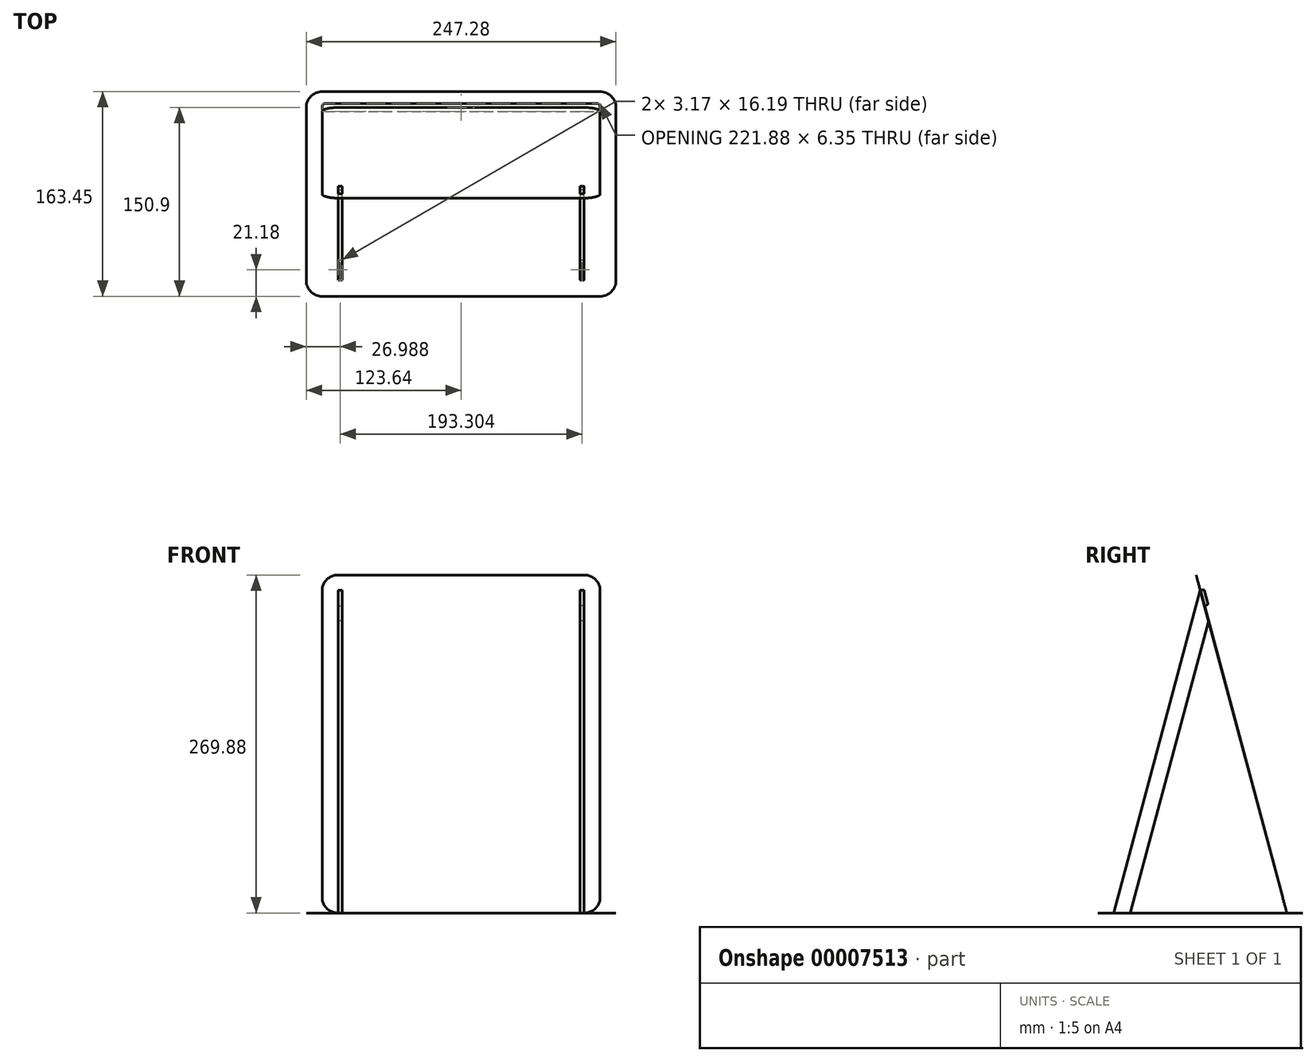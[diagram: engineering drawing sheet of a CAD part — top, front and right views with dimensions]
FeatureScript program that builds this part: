
annotation { "Feature Type Name" : "Feature", "Feature Type Description" : "" }
export const myFeature = defineFeature(function(context is Context, id is Id, definition is map)
    precondition{}
    {
        {
            var Q0;
            Q0=qCreatedBy(makeId("Right.planeOp"),FACE);
            var sketch = newSketch(context, id + "F0", { "sketchPlane" : qUnion([Q0])});
            skLineSegment(sketch, "E0", {"start": v(-72.31, 0) * mm, "end": v(72.31, 0) * mm});
            skLineSegment(sketch, "E1", {"start": v(72.31, 0) * mm, "end": v(0, 269.88) * mm});
            skLineSegment(sketch, "E2", {"start": v(0, 269.88) * mm, "end": v(-72.31, 0) * mm});
            skLineSegment(sketch, "E3", {"start": v(0, 269.88) * mm, "end": v(3.29, 257.61) * mm});
            skLineSegment(sketch, "E4", {"start": v(3.29, 257.61) * mm, "end": v(6.57, 245.35) * mm});
            skLineSegment(sketch, "E5", {"start": v(6.57, 245.35) * mm, "end": v(9.86, 233.08) * mm});
            skLineSegment(sketch, "E6", {"start": v(-72.31, 0) * mm, "end": v(-78.44, 0) * mm});
            skLineSegment(sketch, "E7", {"start": v(72.31, 0) * mm, "end": v(85.01, 0) * mm});
            skLineSegment(sketch, "E8", {"start": v(3.29, 257.61) * mm, "end": v(-65.74, 0) * mm, "construction": true});
            skSolve(sketch);
        }
        {
            var Q0;
            Q0=sQuery(id+"F0.wireOp",EDGE,"E1");
            cPlane(context, id + "F1", {"entities" : qUnion([Q0]), "cplaneType" : CPlaneType.LINE_ANGLE, "offset" : 152.4 * mm, "angle" : 90 * degree, "width" : 152.4 * mm, "height" : 152.4 * mm});
        }
        {
            var Q0;
            Q0=qCreatedBy(id+"F1.planeOp",FACE);
            var sketch = newSketch(context, id + "F2", { "sketchPlane" : qUnion([Q0])});
            skPoint(sketch, "E9.0", {"position": v(0, -18.72) * mm});
            skPoint(sketch, "E9.1", {"position": v(0, 260.68) * mm});
            skLineSegment(sketch, "E10.bottom", {"start": v(-98.24, 260.68) * mm, "end": v(98.24, 260.68) * mm});
            skLineSegment(sketch, "E10.top", {"start": v(-98.24, -18.72) * mm, "end": v(98.24, -18.72) * mm});
            skLineSegment(sketch, "E10.left", {"start": v(-110.94, 247.98) * mm, "end": v(-110.94, -6.02) * mm});
            skLineSegment(sketch, "E10.right", {"start": v(110.94, 247.98) * mm, "end": v(110.94, -6.02) * mm});
            skPoint(sketch, "E11.visualSharp", {"position": v(-110.94, 260.68) * mm});
            skArc(sketch, "E11.filletArc", {"start": v(-98.24, 260.68) * mm, "mid": v(-107.22, 256.96) * mm, "end": v(-110.94, 247.98) * mm});
            skPoint(sketch, "E12.visualSharp", {"position": v(110.94, 260.68) * mm});
            skArc(sketch, "E12.filletArc", {"start": v(110.94, 247.98) * mm, "mid": v(107.22, 256.96) * mm, "end": v(98.24, 260.68) * mm});
            skPoint(sketch, "E13.visualSharp", {"position": v(110.94, -18.72) * mm});
            skArc(sketch, "E13.filletArc", {"start": v(98.24, -18.72) * mm, "mid": v(107.22, -15) * mm, "end": v(110.94, -6.02) * mm});
            skPoint(sketch, "E14.visualSharp", {"position": v(-110.94, -18.72) * mm});
            skArc(sketch, "E14.filletArc", {"start": v(-110.94, -6.02) * mm, "mid": v(-107.22, -15) * mm, "end": v(-98.24, -18.72) * mm});
            skPoint(sketch, "E15.0", {"position": v(0, 247.98) * mm});
            skPoint(sketch, "E15.1", {"position": v(0, 235.28) * mm});
            skLineSegment(sketch, "E16", {"start": v(-98.24, 247.98) * mm, "end": v(98.24, 247.98) * mm, "construction": true});
            skLineSegment(sketch, "E17", {"start": v(-98.24, 235.28) * mm, "end": v(98.24, 235.28) * mm, "construction": true});
            skLineSegment(sketch, "E18", {"start": v(-98.24, 235.28) * mm, "end": v(-98.24, 247.98) * mm});
            skLineSegment(sketch, "E19", {"start": v(-98.24, 235.28) * mm, "end": v(-95.06, 235.28) * mm});
            skLineSegment(sketch, "E20", {"start": v(-95.06, 235.28) * mm, "end": v(-95.06, 247.98) * mm});
            skLineSegment(sketch, "E21", {"start": v(-95.06, 247.98) * mm, "end": v(-98.24, 247.98) * mm});
            skLineSegment(sketch, "E22", {"start": v(98.24, 247.98) * mm, "end": v(98.24, 235.28) * mm});
            skLineSegment(sketch, "E23", {"start": v(98.24, 235.28) * mm, "end": v(95.06, 235.28) * mm});
            skLineSegment(sketch, "E24", {"start": v(95.06, 235.28) * mm, "end": v(95.06, 247.98) * mm});
            skLineSegment(sketch, "E25", {"start": v(95.06, 247.98) * mm, "end": v(98.24, 247.98) * mm});
            skSolve(sketch);
        }
        {
            var Q0;
            Q0=makeQuery(id+"F2.imprint","IMPRINT",FACE,{"disambiguationData":[TD([[makeQuery(id+"F2.imprint","IMPRINT",EDGE,{"derivedFrom":sQuery(id+"F2.wireOp",EDGE,"E10.bottom")}),-1.0]])]});
            extrude(context, id + "F3", {"entities" : qUnion([Q0]), "depth" : 1 / 203.2 * mm});
        }
        {
            var Q0;
            Q0=makeQuery(id+"F3.opExtrude","CAP_EDGE",EDGE,{"disambiguationData":[OSD([sQuery(id+"F2.wireOp",EDGE,"E18")])],"isStart":true});
            cPlane(context, id + "F4", {"entities" : qUnion([Q0]), "cplaneType" : CPlaneType.LINE_ANGLE, "offset" : 152.4 * mm, "angle" : 0 * degree, "width" : 152.4 * mm, "height" : 152.4 * mm});
        }
        {
            var Q0;
            Q0=qCreatedBy(id+"F4.planeOp",FACE);
            var sketch = newSketch(context, id + "F5", { "sketchPlane" : qUnion([Q0])});
            skPoint(sketch, "E26.0", {"position": v(3.29, 257.61) * mm});
            skPoint(sketch, "E26.1", {"position": v(6.57, 245.35) * mm});
            skPoint(sketch, "E26.2", {"position": v(9.86, 233.08) * mm});
            skLineSegment(sketch, "E26.3", {"start": v(-72.31, 0) * mm, "end": v(72.31, 0) * mm, "construction": true});
            skLineSegment(sketch, "E26.4", {"start": v(0, 269.88) * mm, "end": v(-72.31, 0) * mm, "construction": true});
            skLineSegment(sketch, "E27.0", {"start": v(5.13, 258.1) * mm, "end": v(4, 257.8) * mm});
            skLineSegment(sketch, "E28", {"start": v(6.68, 257.2) * mm, "end": v(9.31, 247.4) * mm});
            skLineSegment(sketch, "E29", {"start": v(6.57, 245.35) * mm, "end": v(8.41, 245.84) * mm});
            skLineSegment(sketch, "E30", {"start": v(6.57, 245.35) * mm, "end": v(9.77, 233.4) * mm});
            skLineSegment(sketch, "E31", {"start": v(3.1, 256.9) * mm, "end": v(-65.31, 1.6) * mm});
            skLineSegment(sketch, "E32", {"start": v(-64.08, 0) * mm, "end": v(-53.57, 0) * mm});
            skLineSegment(sketch, "E33", {"start": v(-52.34, 0.94) * mm, "end": v(9.77, 232.75) * mm});
            skPoint(sketch, "E34.visualSharp", {"position": v(6.35, 258.43) * mm});
            skArc(sketch, "E34.filletArc", {"start": v(6.68, 257.2) * mm, "mid": v(6.1, 257.98) * mm, "end": v(5.13, 258.1) * mm});
            skPoint(sketch, "E35.visualSharp", {"position": v(9.64, 246.17) * mm});
            skArc(sketch, "E35.filletArc", {"start": v(8.41, 245.84) * mm, "mid": v(9.19, 246.43) * mm, "end": v(9.31, 247.4) * mm});
            skArc(sketch, "E36.filletArc", {"start": v(9.77, 232.75) * mm, "mid": v(9.82, 233.08) * mm, "end": v(9.77, 233.4) * mm});
            skPoint(sketch, "E37.visualSharp", {"position": v(-52.6, 0) * mm});
            skArc(sketch, "E37.filletArc", {"start": v(-53.57, 0) * mm, "mid": v(-52.8, 0.26) * mm, "end": v(-52.34, 0.94) * mm});
            skLineSegment(sketch, "E38", {"start": v(3.1, 256.9) * mm, "end": v(3.29, 257.61) * mm});
            skLineSegment(sketch, "E39", {"start": v(3.29, 257.61) * mm, "end": v(4, 257.8) * mm});
            skPoint(sketch, "E40.visualSharp", {"position": v(-65.74, 0) * mm});
            skArc(sketch, "E40.filletArc", {"start": v(-65.31, 1.6) * mm, "mid": v(-65.1, 0.5) * mm, "end": v(-64.08, 0) * mm});
            skSolve(sketch);
        }
        {
            var Q0;
            Q0 = qSketchRegion(id + "F5", true);
            var Q1;
            Q1=makeQuery(id+"F3.opExtrude","SWEPT_FACE",FACE,{"disambiguationData":[OSD([sQuery(id+"F2.wireOp",EDGE,"E20")])]});
            extrude(context, id + "F6", {"entities" : qUnion([Q0]), "operationType" : NewBodyOperationType.ADD, "endBound" : BoundingType.UP_TO_SURFACE, "oppositeDirection" : true, "endBoundEntityFace" : qUnion([Q1]), "depth" : 1 / 203.2 * mm});
        }
        {
            var Q0;
            Q0=makeQuery(id+"F3.opExtrude","CAP_EDGE",EDGE,{"disambiguationData":[OSD([sQuery(id+"F2.wireOp",EDGE,"E24")])],"isStart":true});
            cPlane(context, id + "F7", {"entities" : qUnion([Q0]), "cplaneType" : CPlaneType.LINE_ANGLE, "offset" : 152.4 * mm, "angle" : 0 * degree, "width" : 152.4 * mm, "height" : 152.4 * mm});
        }
        {
            var Q0;
            Q0=qCreatedBy(id+"F7.planeOp",FACE);
            var sketch = newSketch(context, id + "F8", { "sketchPlane" : qUnion([Q0])});
            skLineSegment(sketch, "E41.21", {"start": v(3.1, 256.9) * mm, "end": v(3.29, 257.61) * mm});
            skPoint(sketch, "E42.0", {"position": v(3.29, 257.61) * mm});
            skPoint(sketch, "E42.1", {"position": v(6.57, 245.35) * mm});
            skPoint(sketch, "E42.2", {"position": v(9.86, 233.08) * mm});
            skLineSegment(sketch, "E42.3", {"start": v(-72.31, 0) * mm, "end": v(72.31, 0) * mm});
            skLineSegment(sketch, "E42.4", {"start": v(0, 269.88) * mm, "end": v(-72.31, 0) * mm});
            skLineSegment(sketch, "E42.5", {"start": v(5.13, 258.1) * mm, "end": v(4, 257.8) * mm});
            skLineSegment(sketch, "E42.6", {"start": v(6.68, 257.2) * mm, "end": v(9.31, 247.4) * mm});
            skLineSegment(sketch, "E42.7", {"start": v(6.57, 245.35) * mm, "end": v(8.41, 245.84) * mm});
            skLineSegment(sketch, "E42.8", {"start": v(6.57, 245.35) * mm, "end": v(9.77, 233.4) * mm});
            skLineSegment(sketch, "E42.9", {"start": v(3.1, 256.9) * mm, "end": v(-65.31, 1.6) * mm});
            skLineSegment(sketch, "E42.10", {"start": v(-64.08, 0) * mm, "end": v(-53.57, 0) * mm});
            skLineSegment(sketch, "E42.11", {"start": v(-52.34, 0.94) * mm, "end": v(9.77, 232.75) * mm});
            skPoint(sketch, "E42.12", {"position": v(3.29, 257.61) * mm});
            skPoint(sketch, "E42.13", {"position": v(6.35, 258.43) * mm});
            skArc(sketch, "E42.14", {"start": v(6.68, 257.2) * mm, "mid": v(6.1, 257.98) * mm, "end": v(5.13, 258.1) * mm});
            skPoint(sketch, "E42.15", {"position": v(9.64, 246.17) * mm});
            skArc(sketch, "E42.16", {"start": v(8.41, 245.84) * mm, "mid": v(9.19, 246.43) * mm, "end": v(9.31, 247.4) * mm});
            skPoint(sketch, "E42.17", {"position": v(9.86, 233.08) * mm});
            skArc(sketch, "E42.18", {"start": v(9.77, 232.75) * mm, "mid": v(9.82, 233.08) * mm, "end": v(9.77, 233.4) * mm});
            skPoint(sketch, "E42.19", {"position": v(-52.6, 0) * mm});
            skArc(sketch, "E42.20", {"start": v(-53.57, 0) * mm, "mid": v(-52.8, 0.26) * mm, "end": v(-52.34, 0.94) * mm});
            skLineSegment(sketch, "E42.22", {"start": v(3.29, 257.61) * mm, "end": v(4, 257.8) * mm});
            skPoint(sketch, "E42.23", {"position": v(-65.74, 0) * mm});
            skArc(sketch, "E42.24", {"start": v(-65.31, 1.6) * mm, "mid": v(-65.1, 0.5) * mm, "end": v(-64.08, 0) * mm});
            skSolve(sketch);
        }
        {
            var Q0;
            Q0 = qSketchRegion(id + "F8", true);
            var Q1;
            Q1=makeQuery(id+"F3.opExtrude","SWEPT_FACE",FACE,{"disambiguationData":[OSD([sQuery(id+"F2.wireOp",EDGE,"E22")])]});
            extrude(context, id + "F9", {"entities" : qUnion([Q0]), "operationType" : NewBodyOperationType.ADD, "endBound" : BoundingType.UP_TO_SURFACE, "oppositeDirection" : true, "endBoundEntityFace" : qUnion([Q1]), "depth" : 3.17 * mm});
        }
        {
            var Q0;
            Q0=qCreatedBy(makeId("Top.planeOp"),FACE);
            var sketch = newSketch(context, id + "F10", { "sketchPlane" : qUnion([Q0])});
            skPoint(sketch, "E43.2", {"position": v(0, 85.01) * mm});
            skPoint(sketch, "E43.3", {"position": v(0, -78.44) * mm});
            skLineSegment(sketch, "E44.bottom", {"start": v(-110.94, -78.44) * mm, "end": v(110.94, -78.44) * mm});
            skLineSegment(sketch, "E44.top", {"start": v(-110.94, 85.01) * mm, "end": v(110.94, 85.01) * mm});
            skLineSegment(sketch, "E44.left", {"start": v(-123.64, -65.74) * mm, "end": v(-123.64, 72.31) * mm});
            skLineSegment(sketch, "E44.right", {"start": v(123.64, -65.74) * mm, "end": v(123.64, 72.31) * mm});
            skPoint(sketch, "E45.visualSharp", {"position": v(-123.64, -78.44) * mm});
            skArc(sketch, "E45.filletArc", {"start": v(-123.64, -65.74) * mm, "mid": v(-119.92, -74.72) * mm, "end": v(-110.94, -78.44) * mm});
            skPoint(sketch, "E46.visualSharp", {"position": v(123.64, -78.44) * mm});
            skArc(sketch, "E46.filletArc", {"start": v(110.94, -78.44) * mm, "mid": v(119.92, -74.72) * mm, "end": v(123.64, -65.74) * mm});
            skPoint(sketch, "E47.visualSharp", {"position": v(123.64, 85.01) * mm});
            skArc(sketch, "E47.filletArc", {"start": v(123.64, 72.31) * mm, "mid": v(119.92, 81.3) * mm, "end": v(110.94, 85.01) * mm});
            skPoint(sketch, "E48.visualSharp", {"position": v(-123.64, 85.01) * mm});
            skArc(sketch, "E48.filletArc", {"start": v(-110.94, 85.01) * mm, "mid": v(-119.92, 81.3) * mm, "end": v(-123.64, 72.31) * mm});
            skLineSegment(sketch, "E49.0", {"start": v(98.24, 75.38) * mm, "end": v(-98.24, 75.38) * mm, "construction": true});
            skLineSegment(sketch, "E50.bottom", {"start": v(-108.4, 69.28) * mm, "end": v(108.4, 69.28) * mm});
            skLineSegment(sketch, "E50.top", {"start": v(-108.4, 75.63) * mm, "end": v(108.4, 75.63) * mm});
            skLineSegment(sketch, "E50.left", {"start": v(-110.94, 71.82) * mm, "end": v(-110.94, 73.1) * mm});
            skLineSegment(sketch, "E50.right", {"start": v(110.94, 71.82) * mm, "end": v(110.94, 73.1) * mm});
            skPoint(sketch, "E51.visualSharp", {"position": v(-110.94, 69.28) * mm});
            skArc(sketch, "E51.filletArc", {"start": v(-110.94, 71.82) * mm, "mid": v(-110.2, 70.03) * mm, "end": v(-108.4, 69.28) * mm});
            skPoint(sketch, "E52.visualSharp", {"position": v(-110.94, 75.63) * mm});
            skArc(sketch, "E52.filletArc", {"start": v(-108.4, 75.63) * mm, "mid": v(-110.2, 74.9) * mm, "end": v(-110.94, 73.1) * mm});
            skPoint(sketch, "E53.visualSharp", {"position": v(110.94, 75.63) * mm});
            skArc(sketch, "E53.filletArc", {"start": v(110.94, 73.1) * mm, "mid": v(110.2, 74.9) * mm, "end": v(108.4, 75.63) * mm});
            skPoint(sketch, "E54.visualSharp", {"position": v(110.94, 69.28) * mm});
            skArc(sketch, "E54.filletArc", {"start": v(108.4, 69.28) * mm, "mid": v(110.2, 70.03) * mm, "end": v(110.94, 71.82) * mm});
            skLineSegment(sketch, "E55.0", {"start": v(-98.24, -64.08) * mm, "end": v(-98.24, -65.35) * mm});
            skLineSegment(sketch, "E55.1", {"start": v(-95.06, -64.08) * mm, "end": v(-95.06, -65.35) * mm});
            skLineSegment(sketch, "E55.2", {"start": v(-95.06, -64.08) * mm, "end": v(-95.06, -53.57) * mm});
            skLineSegment(sketch, "E55.3", {"start": v(-95.06, -52.34) * mm, "end": v(-95.06, -53.57) * mm});
            skLineSegment(sketch, "E55.4", {"start": v(-98.24, -64.08) * mm, "end": v(-98.24, -53.57) * mm});
            skLineSegment(sketch, "E55.5", {"start": v(-98.24, -52.34) * mm, "end": v(-98.24, -53.57) * mm});
            skLineSegment(sketch, "E56", {"start": v(-98.24, -65.35) * mm, "end": v(-95.06, -65.35) * mm});
            skLineSegment(sketch, "E57", {"start": v(-98.24, -52.34) * mm, "end": v(-98.24, -49.16) * mm});
            skLineSegment(sketch, "E58", {"start": v(-98.24, -49.16) * mm, "end": v(-95.06, -49.16) * mm});
            skLineSegment(sketch, "E59", {"start": v(-95.06, -49.16) * mm, "end": v(-95.06, -52.34) * mm});
            skLineSegment(sketch, "E60.0", {"start": v(95.06, -53.57) * mm, "end": v(95.06, -64.08) * mm});
            skLineSegment(sketch, "E60.1", {"start": v(95.06, -65.35) * mm, "end": v(95.06, -64.08) * mm});
            skLineSegment(sketch, "E60.2", {"start": v(98.24, -64.08) * mm, "end": v(98.24, -65.35) * mm});
            skLineSegment(sketch, "E60.3", {"start": v(98.24, -64.08) * mm, "end": v(98.24, -53.57) * mm});
            skLineSegment(sketch, "E60.4", {"start": v(95.06, -53.57) * mm, "end": v(95.06, -52.34) * mm});
            skLineSegment(sketch, "E60.5", {"start": v(98.24, -52.34) * mm, "end": v(98.24, -53.57) * mm});
            skLineSegment(sketch, "E61", {"start": v(95.06, -65.35) * mm, "end": v(98.24, -65.35) * mm});
            skLineSegment(sketch, "E62", {"start": v(95.06, -52.34) * mm, "end": v(95.06, -49.16) * mm});
            skLineSegment(sketch, "E63", {"start": v(95.06, -49.16) * mm, "end": v(98.24, -49.16) * mm});
            skLineSegment(sketch, "E64", {"start": v(98.24, -49.16) * mm, "end": v(98.24, -52.34) * mm});
            skSolve(sketch);
        }
        {
            var Q0;
            Q0 = qSketchRegion(id + "F10", true);
            extrude(context, id + "F11", {"entities" : qUnion([Q0]), "operationType" : NewBodyOperationType.ADD, "oppositeDirection" : true, "depth" : 1 / 203.2 * mm});
        }
    });
